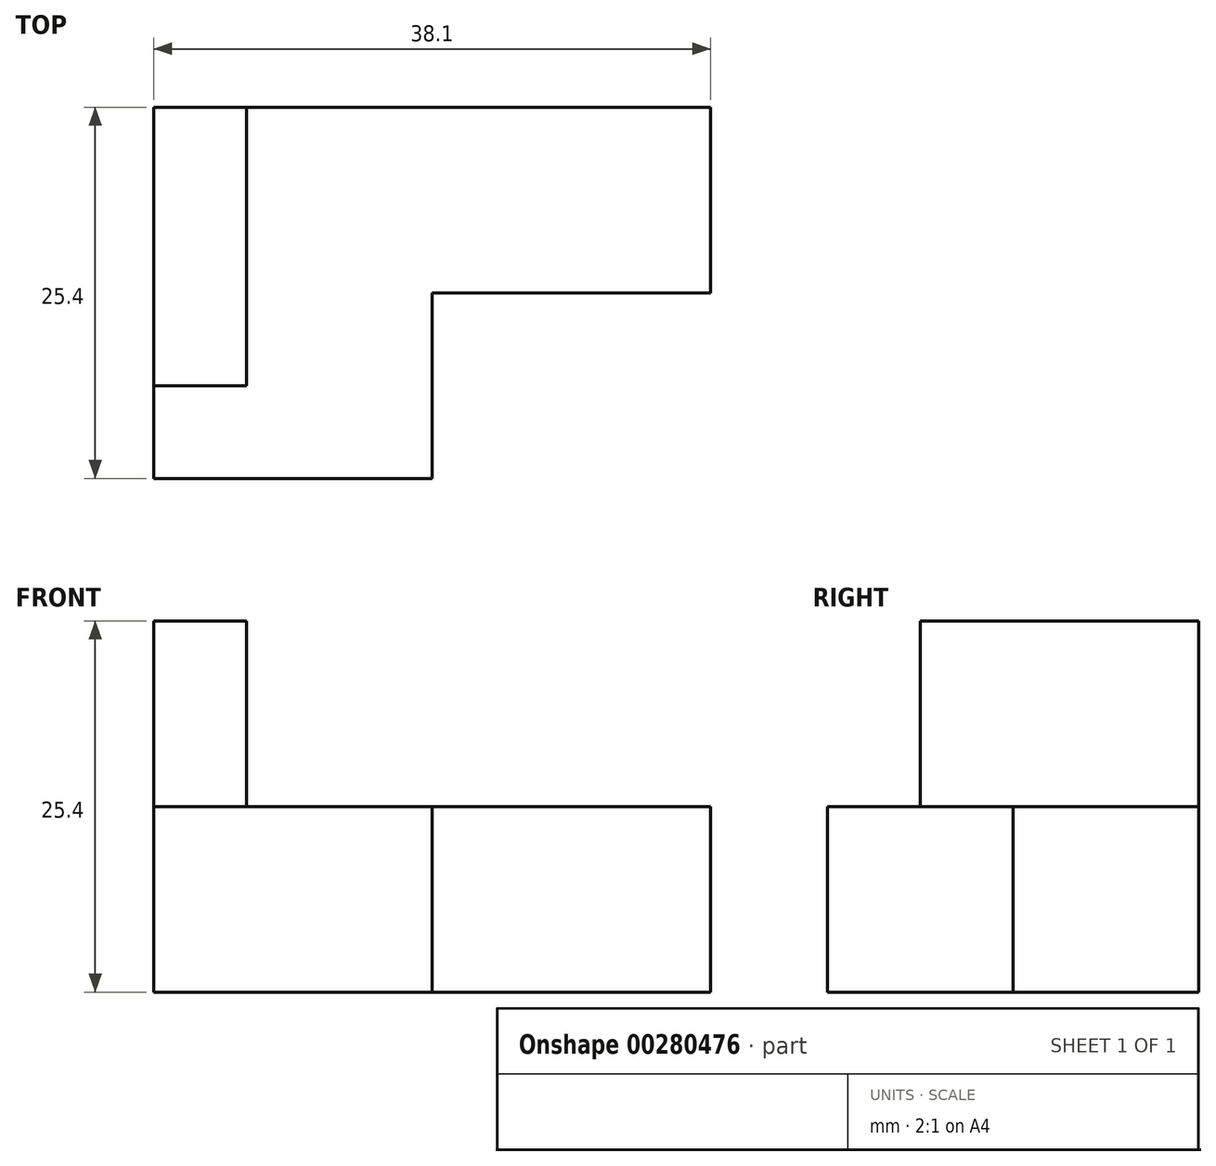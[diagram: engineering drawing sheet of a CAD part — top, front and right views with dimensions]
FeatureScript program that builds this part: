
annotation { "Feature Type Name" : "Feature", "Feature Type Description" : "" }
export const myFeature = defineFeature(function(context is Context, id is Id, definition is map)
    precondition{}
    {
        {
            var Q0;
            Q0=qCreatedBy(makeId("Front.planeOp"),FACE);
            var sketch = newSketch(context, id + "F0", { "sketchPlane" : qUnion([Q0])});
            skLineSegment(sketch, "E0.bottom", {"start": v(0, 0) * mm, "end": v(38.1, 0) * mm});
            skLineSegment(sketch, "E0.top", {"start": v(0, 12.7) * mm, "end": v(38.1, 12.7) * mm});
            skLineSegment(sketch, "E0.left", {"start": v(0, 0) * mm, "end": v(0, 12.7) * mm});
            skLineSegment(sketch, "E0.right", {"start": v(38.1, 0) * mm, "end": v(38.1, 12.7) * mm});
            skSolve(sketch);
        }
        {
            var Q0;
            Q0 = qSketchRegion(id + "F0", true);
            extrude(context, id + "F1", {"entities" : qUnion([Q0]), "depth" : 25.4 * mm});
        }
        {
            var Q0;
            Q0=qCreatedBy(makeId("Front.planeOp"),FACE);
            var sketch = newSketch(context, id + "F2", { "sketchPlane" : qUnion([Q0])});
            skLineSegment(sketch, "E1", {"start": v(0, 12.7) * mm, "end": v(0, 25.4) * mm});
            skLineSegment(sketch, "E2", {"start": v(0, 25.4) * mm, "end": v(6.35, 25.4) * mm});
            skLineSegment(sketch, "E3", {"start": v(6.35, 25.4) * mm, "end": v(6.35, 12.7) * mm});
            skLineSegment(sketch, "E4", {"start": v(6.35, 12.7) * mm, "end": v(0, 12.7) * mm});
            skSolve(sketch);
        }
        {
            var Q0;
            Q0 = qSketchRegion(id + "F2", true);
            extrude(context, id + "F3", {"entities" : qUnion([Q0]), "operationType" : NewBodyOperationType.ADD, "depth" : 19.05 * mm});
        }
        {
            var Q0;
            Q0=makeQuery(id+"F1.opExtrude","CAP_FACE",FACE,{"disambiguationData":[OSD([sQuery(id+"F0.wireOp",EDGE,"E0.bottom"),sQuery(id+"F0.wireOp",EDGE,"E0.top"),sQuery(id+"F0.wireOp",EDGE,"E0.left"),sQuery(id+"F0.wireOp",EDGE,"E0.right")])],"isStart":false});
            var sketch = newSketch(context, id + "F4", { "sketchPlane" : qUnion([Q0])});
            skLineSegment(sketch, "E5", {"start": v(19.05, 12.7) * mm, "end": v(38.1, 12.7) * mm});
            skLineSegment(sketch, "E6", {"start": v(38.1, 12.7) * mm, "end": v(38.1, 0) * mm});
            skLineSegment(sketch, "E7", {"start": v(38.1, 0) * mm, "end": v(19.05, 0) * mm});
            skLineSegment(sketch, "E8", {"start": v(19.05, 0) * mm, "end": v(19.05, 12.7) * mm});
            skSolve(sketch);
        }
        {
            var Q0;
            Q0 = qSketchRegion(id + "F4", true);
            extrude(context, id + "F5", {"entities" : qUnion([Q0]), "operationType" : NewBodyOperationType.REMOVE, "oppositeDirection" : true, "depth" : 12.7 * mm});
        }
    });
